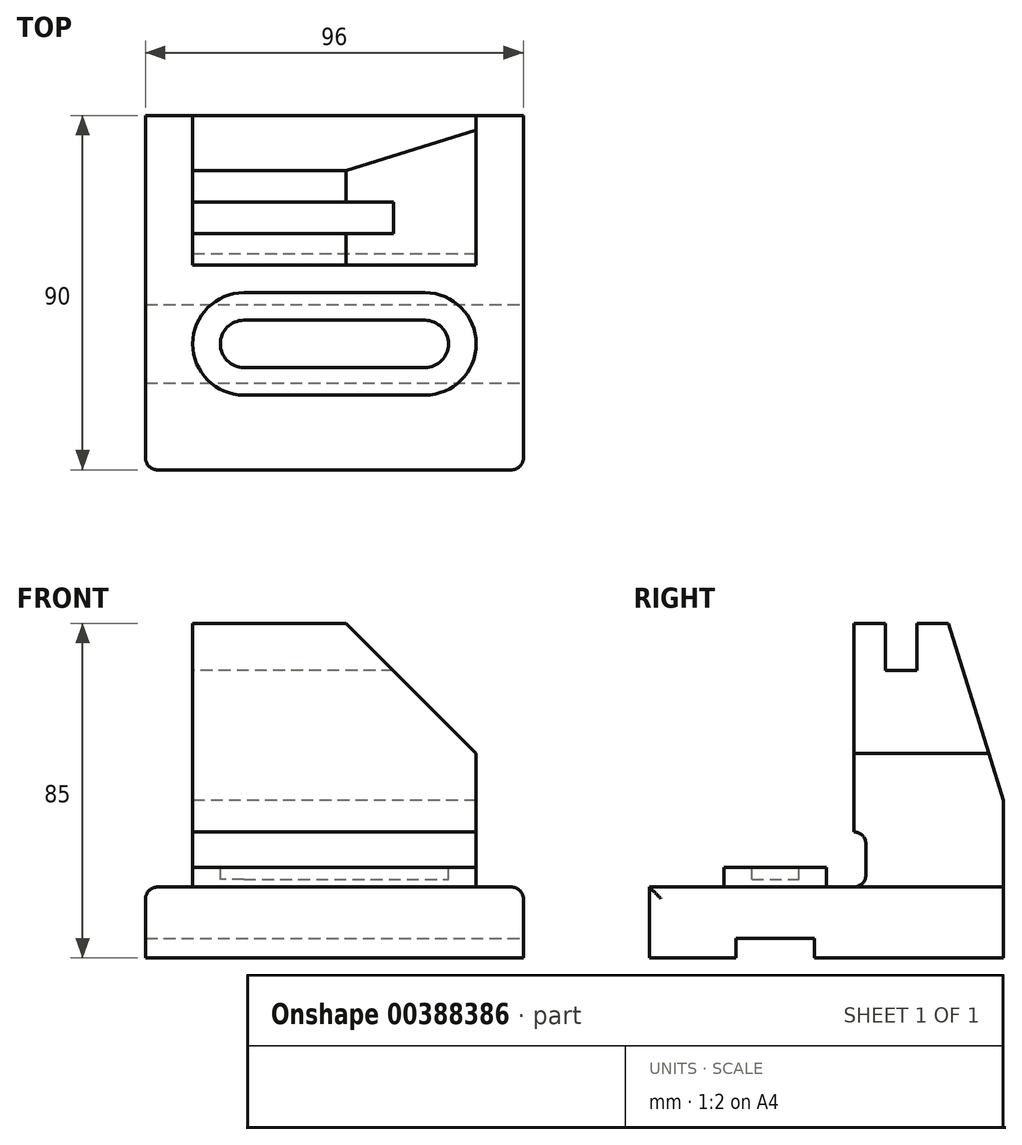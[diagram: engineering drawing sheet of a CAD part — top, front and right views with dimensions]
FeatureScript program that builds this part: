
annotation { "Feature Type Name" : "Feature", "Feature Type Description" : "" }
export const myFeature = defineFeature(function(context is Context, id is Id, definition is map)
    precondition{}
    {
        {
            var Q0;
            Q0=qCreatedBy(makeId("Top.planeOp"),FACE);
            var sketch = newSketch(context, id + "F0", { "sketchPlane" : qUnion([Q0])});
            skLineSegment(sketch, "E0.bottom", {"start": v(0, 0) * mm, "end": v(96, 0) * mm});
            skLineSegment(sketch, "E0.top", {"start": v(0, 90) * mm, "end": v(96, 90) * mm});
            skLineSegment(sketch, "E0.left", {"start": v(0, 0) * mm, "end": v(0, 90) * mm});
            skLineSegment(sketch, "E0.right", {"start": v(96, 0) * mm, "end": v(96, 90) * mm});
            skSolve(sketch);
        }
        {
            var Q0;
            Q0 = qSketchRegion(id + "F0", true);
            extrude(context, id + "F1", {"entities" : qUnion([Q0]), "depth" : 18 * mm});
        }
        {
            var Q0;
            Q0=makeQuery(id+"F1.opExtrude","CAP_FACE",FACE,{"disambiguationData":[OSD([sQuery(id+"F0.wireOp",EDGE,"E0.bottom"),sQuery(id+"F0.wireOp",EDGE,"E0.top"),sQuery(id+"F0.wireOp",EDGE,"E0.left"),sQuery(id+"F0.wireOp",EDGE,"E0.right")])],"isStart":false});
            var sketch = newSketch(context, id + "F2", { "sketchPlane" : qUnion([Q0])});
            skLineSegment(sketch, "E1.bottom", {"start": v(84, 90) * mm, "end": v(12, 90) * mm});
            skLineSegment(sketch, "E1.top", {"start": v(84, 52) * mm, "end": v(12, 52) * mm});
            skLineSegment(sketch, "E1.left", {"start": v(84, 90) * mm, "end": v(84, 52) * mm});
            skLineSegment(sketch, "E1.right", {"start": v(12, 90) * mm, "end": v(12, 52) * mm});
            skSolve(sketch);
        }
        {
            var Q0;
            Q0=makeQuery(id+"F1.opExtrude","CAP_FACE",FACE,{"disambiguationData":[OSD([sQuery(id+"F0.wireOp",EDGE,"E0.bottom"),sQuery(id+"F0.wireOp",EDGE,"E0.top"),sQuery(id+"F0.wireOp",EDGE,"E0.left"),sQuery(id+"F0.wireOp",EDGE,"E0.right")])],"isStart":true});
            cPlane(context, id + "F3", {"entities" : qUnion([Q0]), "cplaneType" : CPlaneType.OFFSET, "offset" : 85 * mm, "oppositeDirection" : true, "width" : 150 * mm, "height" : 150 * mm});
        }
        {
            var Q0;
            Q0 = qSketchRegion(id + "F2", true);
            var Q1;
            Q1=qCreatedBy(id+"F3.planeOp",FACE);
            extrude(context, id + "F4", {"entities" : qUnion([Q0]), "operationType" : NewBodyOperationType.ADD, "endBound" : BoundingType.UP_TO_SURFACE, "endBoundEntityFace" : qUnion([Q1]), "depth" : (16 - 78) * mm});
        }
        {
            var Q0;
            Q0=makeQuery(id+"F4.opExtrude","SWEPT_FACE",FACE,{"disambiguationData":[OSD([sQuery(id+"F2.wireOp",EDGE,"E1.top")])]});
            var sketch = newSketch(context, id + "F5", { "sketchPlane" : qUnion([Q0])});
            skLineSegment(sketch, "E2", {"start": v(84, 85) * mm, "end": v(51, 85) * mm});
            skLineSegment(sketch, "E3", {"start": v(51, 85) * mm, "end": v(84, 52) * mm});
            skSolve(sketch);
        }
        {
            var Q0;
            Q0 = qSketchRegion(id + "F5", true);
            var Q1;
            {var subQ0=sQuery(id+"F5.wireOp",EDGE,"E2");Q1=makeQuery(id+"F5.imprint","IMPRINT",FACE,{"disambiguationData":[TD([[makeQuery(id+"F5.imprint","IMPRINT",EDGE,{"derivedFrom":subQ0}),-1.0]])]});}
            var Q2;
            Q2=makeQuery(id+"F4.boolean.opBoolean","MERGE",FACE,{"derivedFrom":[makeQuery(id+"F1.opExtrude","SWEPT_FACE",FACE,{"disambiguationData":[OSD([sQuery(id+"F0.wireOp",EDGE,"E0.top")])]}),makeQuery(id+"F4.opExtrude","SWEPT_FACE",FACE,{"disambiguationData":[OSD([sQuery(id+"F2.wireOp",EDGE,"E1.bottom")])]})]});
            extrude(context, id + "F6", {"entities" : qUnion([Q0, Q1]), "operationType" : NewBodyOperationType.REMOVE, "endBound" : BoundingType.UP_TO_SURFACE, "oppositeDirection" : true, "endBoundEntityFace" : qUnion([Q2]), "depth" : 25 * mm});
        }
        {
            var Q0;
            Q0=makeQuery(id+"F4.opExtrude","SWEPT_FACE",FACE,{"disambiguationData":[OSD([sQuery(id+"F2.wireOp",EDGE,"E1.right")])]});
            var sketch = newSketch(context, id + "F7", { "sketchPlane" : qUnion([Q0])});
            skLineSegment(sketch, "E4.bottom", {"start": v(-68, 85) * mm, "end": v(-60, 85) * mm});
            skLineSegment(sketch, "E4.top", {"start": v(-68, 73) * mm, "end": v(-60, 73) * mm});
            skLineSegment(sketch, "E4.left", {"start": v(-68, 85) * mm, "end": v(-68, 73) * mm});
            skLineSegment(sketch, "E4.right", {"start": v(-60, 85) * mm, "end": v(-60, 73) * mm});
            skSolve(sketch);
        }
        {
            var Q0;
            Q0 = qSketchRegion(id + "F7", true);
            extrude(context, id + "F8", {"entities" : qUnion([Q0]), "operationType" : NewBodyOperationType.REMOVE, "endBound" : BoundingType.UP_TO_NEXT, "oppositeDirection" : true, "depth" : 25 * mm});
        }
        {
            var Q0;
            Q0=makeQuery(id+"F4.opExtrude","SWEPT_FACE",FACE,{"disambiguationData":[OSD([sQuery(id+"F2.wireOp",EDGE,"E1.right")])]});
            var sketch = newSketch(context, id + "F9", { "sketchPlane" : qUnion([Q0])});
            skLineSegment(sketch, "E5", {"start": v(-76, 85) * mm, "end": v(-90, 40) * mm});
            skSolve(sketch);
        }
        {
            var Q0;
            Q0 = qSketchRegion(id + "F9", true);
            var Q1;
            {var subQ0=sQuery(id+"F9.wireOp",EDGE,"E5");Q1=makeQuery(id+"F9.imprint","IMPRINT",FACE,{"disambiguationData":[TD([[makeQuery(id+"F9.imprint","IMPRINT",EDGE,{"derivedFrom":subQ0}),-1.0]])]});}
            extrude(context, id + "F10", {"entities" : qUnion([Q0, Q1]), "operationType" : NewBodyOperationType.REMOVE, "endBound" : BoundingType.UP_TO_NEXT, "oppositeDirection" : true, "depth" : 25 * mm});
        }
        {
            var Q0;
            Q0=makeQuery(id+"F1.opExtrude","SWEPT_FACE",FACE,{"disambiguationData":[OSD([sQuery(id+"F0.wireOp",EDGE,"E0.right")])]});
            var sketch = newSketch(context, id + "F11", { "sketchPlane" : qUnion([Q0])});
            skLineSegment(sketch, "E6.bottom", {"start": v(42, 0) * mm, "end": v(22, 0) * mm});
            skLineSegment(sketch, "E6.top", {"start": v(42, 5) * mm, "end": v(22, 5) * mm});
            skLineSegment(sketch, "E6.left", {"start": v(42, 0) * mm, "end": v(42, 5) * mm});
            skLineSegment(sketch, "E6.right", {"start": v(22, 0) * mm, "end": v(22, 5) * mm});
            skPoint(sketch, "E7", {"position": v(32, 5) * mm});
            skSolve(sketch);
        }
        {
            var Q0;
            Q0 = qSketchRegion(id + "F11", true);
            extrude(context, id + "F12", {"entities" : qUnion([Q0]), "operationType" : NewBodyOperationType.REMOVE, "endBound" : BoundingType.UP_TO_NEXT, "oppositeDirection" : true, "depth" : 25 * mm});
        }
        {
            var Q0;
            Q0=makeQuery(id+"F1.opExtrude","CAP_FACE",FACE,{"disambiguationData":[OSD([sQuery(id+"F0.wireOp",EDGE,"E0.bottom"),sQuery(id+"F0.wireOp",EDGE,"E0.top"),sQuery(id+"F0.wireOp",EDGE,"E0.left"),sQuery(id+"F0.wireOp",EDGE,"E0.right")])],"isStart":false});
            var sketch = newSketch(context, id + "F13", { "sketchPlane" : qUnion([Q0])});
            skLineSegment(sketch, "E8.bottom", {"start": v(25, 45) * mm, "end": v(71, 45) * mm});
            skLineSegment(sketch, "E8.top", {"start": v(25, 19) * mm, "end": v(71, 19) * mm});
            skLineSegment(sketch, "E8.left", {"start": v(25, 45) * mm, "end": v(25, 19) * mm});
            skLineSegment(sketch, "E8.right", {"start": v(71, 45) * mm, "end": v(71, 19) * mm});
            skLineSegment(sketch, "E9", {"start": v(25, 32) * mm, "end": v(71, 32) * mm, "construction": true});
            skArc(sketch, "E10", {"start": v(25, 45) * mm, "mid": v(12, 32) * mm, "end": v(25, 19) * mm});
            skArc(sketch, "E11", {"start": v(71, 19) * mm, "mid": v(84, 32) * mm, "end": v(71, 45) * mm});
            skSolve(sketch);
        }
        {
            var Q0;
            Q0 = qSketchRegion(id + "F13", true);
            extrude(context, id + "F14", {"entities" : qUnion([Q0]), "operationType" : NewBodyOperationType.ADD, "depth" : 5 * mm});
        }
        {
            var Q0;
            Q0=makeQuery(id+"F14.opExtrude","CAP_FACE",FACE,{"disambiguationData":[OSD([sQuery(id+"F13.wireOp",EDGE,"E8.bottom"),sQuery(id+"F13.wireOp",EDGE,"E8.top"),sQuery(id+"F13.wireOp",EDGE,"E10"),sQuery(id+"F13.wireOp",EDGE,"E11")])],"isStart":false});
            var sketch = newSketch(context, id + "F15", { "sketchPlane" : qUnion([Q0])});
            skLineSegment(sketch, "E12", {"start": v(25, 32) * mm, "end": v(25, 38) * mm});
            skLineSegment(sketch, "E13", {"start": v(25, 38) * mm, "end": v(71, 38) * mm});
            skLineSegment(sketch, "E14", {"start": v(71, 38) * mm, "end": v(71, 26) * mm});
            skLineSegment(sketch, "E15", {"start": v(71, 26) * mm, "end": v(25, 26) * mm});
            skLineSegment(sketch, "E16", {"start": v(25, 26) * mm, "end": v(25, 32) * mm});
            skArc(sketch, "E17", {"start": v(25, 38) * mm, "mid": v(19, 32) * mm, "end": v(25, 26) * mm});
            skArc(sketch, "E18", {"start": v(71, 26) * mm, "mid": v(77, 32) * mm, "end": v(71, 38) * mm});
            skSolve(sketch);
        }
        {
            var Q0;
            Q0=makeQuery(id+"F15.imprint","IMPRINT",FACE,{"disambiguationData":[TD([[makeQuery(id+"F15.imprint","IMPRINT",EDGE,{"derivedFrom":sQuery(id+"F15.wireOp",EDGE,"E14")}),1.0]])]});
            var Q1;
            Q1=makeQuery(id+"F15.imprint","IMPRINT",FACE,{"disambiguationData":[TD([[makeQuery(id+"F15.imprint","IMPRINT",EDGE,{"derivedFrom":sQuery(id+"F15.wireOp",EDGE,"E12")}),-1.0]])]});
            var Q2;
            Q2=makeQuery(id+"F15.imprint","IMPRINT",FACE,{"disambiguationData":[TD([[makeQuery(id+"F15.imprint","IMPRINT",EDGE,{"derivedFrom":sQuery(id+"F15.wireOp",EDGE,"E12")}),1.0]])]});
            extrude(context, id + "F16", {"entities" : qUnion([Q0, Q1, Q2]), "operationType" : NewBodyOperationType.REMOVE, "oppositeDirection" : true, "depth" : 3 * mm});
        }
        {
            var Q0;
            Q0=makeQuery(id+"F4.opExtrude","SWEPT_FACE",FACE,{"disambiguationData":[OSD([sQuery(id+"F2.wireOp",EDGE,"E1.left")])]});
            var sketch = newSketch(context, id + "F17", { "sketchPlane" : qUnion([Q0])});
            skLineSegment(sketch, "E19.bottom", {"start": v(52, 18) * mm, "end": v(55, 18) * mm});
            skLineSegment(sketch, "E19.top", {"start": v(52, 32) * mm, "end": v(55, 32) * mm});
            skLineSegment(sketch, "E19.left", {"start": v(52, 18) * mm, "end": v(52, 32) * mm});
            skLineSegment(sketch, "E19.right", {"start": v(55, 18) * mm, "end": v(55, 32) * mm});
            skSolve(sketch);
        }
        {
            var Q0;
            Q0 = qSketchRegion(id + "F17", true);
            extrude(context, id + "F18", {"entities" : qUnion([Q0]), "operationType" : NewBodyOperationType.REMOVE, "endBound" : BoundingType.UP_TO_NEXT, "oppositeDirection" : true, "depth" : 25 * mm});
        }
        {
            var Q0;
            Q0=makeQuery(id+"F18.boolean.opBoolean","COPY",EDGE,{"derivedFrom":makeQuery(id+"F18.opExtrude","SWEPT_EDGE",EDGE,{"disambiguationData":[OSD([sQuery(id+"F2.wireOp",EDGE,"E1.left"),sQuery(id+"F17.wireOp",EDGE,"E19.bottom"),sQuery(id+"F17.wireOp",EDGE,"E19.right")])]})});
            var Q1;
            Q1=makeQuery(id+"F14.opExtrude","CAP_EDGE",EDGE,{"disambiguationData":[OSD([sQuery(id+"F13.wireOp",EDGE,"E8.top")])],"isStart":true});
            var Q2;
            Q2=makeQuery(id+"F18.boolean.opBoolean","COPY",EDGE,{"derivedFrom":makeQuery(id+"F18.opExtrude","SWEPT_EDGE",EDGE,{"disambiguationData":[OSD([sQuery(id+"F17.wireOp",EDGE,"E19.top"),sQuery(id+"F17.wireOp",EDGE,"E19.right")])]})});
            var Q3;
            Q3=makeQuery(id+"F1.opExtrude","CAP_EDGE",EDGE,{"disambiguationData":[OSD([sQuery(id+"F0.wireOp",EDGE,"E0.right")])],"isStart":false});
            var Q4;
            Q4=makeQuery(id+"F1.opExtrude","CAP_EDGE",EDGE,{"disambiguationData":[OSD([sQuery(id+"F0.wireOp",EDGE,"E0.left")])],"isStart":false});
            var Q5;
            Q5=makeQuery(id+"F1.opExtrude","SWEPT_EDGE",EDGE,{"disambiguationData":[OSD([sQuery(id+"F0.wireOp",EDGE,"E0.bottom"),sQuery(id+"F0.wireOp",EDGE,"E0.right")])]});
            var Q6;
            Q6=makeQuery(id+"F1.opExtrude","SWEPT_EDGE",EDGE,{"disambiguationData":[OSD([sQuery(id+"F0.wireOp",EDGE,"E0.bottom"),sQuery(id+"F0.wireOp",EDGE,"E0.left")])]});
            fillet(context, id + "F19", {"entities" : qUnion([Q0, Q1, Q2, Q3, Q4, Q5, Q6]), "radius" : 3 * mm, "tangentPropagation" : true, "allowEdgeOverflow" : false});
        }
    });
